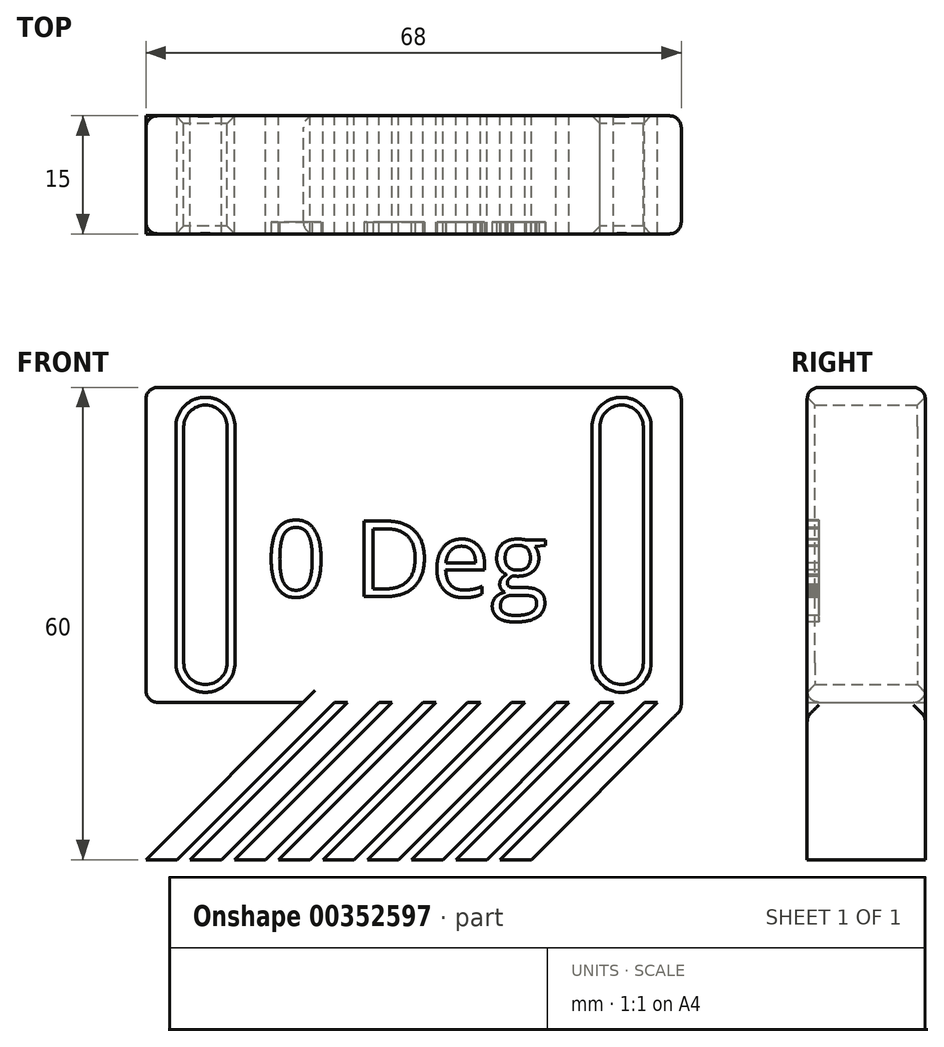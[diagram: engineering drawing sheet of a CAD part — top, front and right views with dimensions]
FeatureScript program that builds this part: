
annotation { "Feature Type Name" : "Feature", "Feature Type Description" : "" }
export const myFeature = defineFeature(function(context is Context, id is Id, definition is map)
    precondition{}
    {
        {
            var Q0;
            Q0=qCreatedBy(makeId("Front.planeOp"),FACE);
            var sketch = newSketch(context, id + "F0", { "sketchPlane" : qUnion([Q0])});
            skLineSegment(sketch, "E0.top", {"start": v(34, 30) * mm, "end": v(-34, 30) * mm});
            skLineSegment(sketch, "E0.left", {"start": v(34, -10.96) * mm, "end": v(34, 30) * mm});
            skLineSegment(sketch, "E0.right", {"start": v(-34, -10) * mm, "end": v(-34, 30) * mm});
            skPoint(sketch, "E0.middle", {"position": v(0, 0) * mm});
            skLineSegment(sketch, "E1", {"start": v(-34, -30) * mm, "end": v(-14, -10) * mm});
            skLineSegment(sketch, "E2", {"start": v(-10.04, -10) * mm, "end": v(-30.04, -30) * mm});
            skLineSegment(sketch, "E3.1.0.0", {"start": v(-28.38, -30) * mm, "end": v(-8.37, -10) * mm});
            skLineSegment(sketch, "E3.1.0.1", {"start": v(-4.42, -10) * mm, "end": v(-24.42, -30) * mm});
            skLineSegment(sketch, "E3.2.0.0", {"start": v(-22.75, -30) * mm, "end": v(-2.75, -10) * mm});
            skLineSegment(sketch, "E3.2.0.1", {"start": v(1.2, -10) * mm, "end": v(-18.8, -30) * mm});
            skLineSegment(sketch, "E3.3.0.0", {"start": v(-17.12, -30) * mm, "end": v(2.88, -10) * mm});
            skLineSegment(sketch, "E3.3.0.1", {"start": v(6.83, -10) * mm, "end": v(-13.17, -30) * mm});
            skLineSegment(sketch, "E3.4.0.0", {"start": v(-11.5, -30) * mm, "end": v(8.5, -10) * mm});
            skLineSegment(sketch, "E3.4.0.1", {"start": v(12.46, -10) * mm, "end": v(-7.54, -30) * mm});
            skLineSegment(sketch, "E3.5.0.0", {"start": v(-5.87, -30) * mm, "end": v(14.13, -10) * mm});
            skLineSegment(sketch, "E3.5.0.1", {"start": v(18.08, -10) * mm, "end": v(-1.92, -30) * mm});
            skLineSegment(sketch, "E3.6.0.0", {"start": v(-0.25, -30) * mm, "end": v(19.75, -10) * mm});
            skLineSegment(sketch, "E3.6.0.1", {"start": v(23.7, -10) * mm, "end": v(3.7, -30) * mm});
            skLineSegment(sketch, "E3.7.0.0", {"start": v(5.38, -30) * mm, "end": v(25.38, -10) * mm});
            skLineSegment(sketch, "E3.7.0.1", {"start": v(29.33, -10) * mm, "end": v(9.33, -30) * mm});
            skLineSegment(sketch, "E3.8.0.0", {"start": v(11, -30) * mm, "end": v(31, -10) * mm});
            skLineSegment(sketch, "E3.8.0.1", {"start": v(34, -10.96) * mm, "end": v(14.96, -30) * mm});
            skLineSegment(sketch, "E3.direction1", {"start": v(-34, -30) * mm, "end": v(-30.04, -30) * mm, "construction": true});
            skLineSegment(sketch, "E4.trimOffspring", {"start": v(-24.42, -30) * mm, "end": v(-28.37, -30) * mm});
            skLineSegment(sketch, "E5.trimOffspring", {"start": v(-30.04, -30) * mm, "end": v(-34, -30) * mm});
            skLineSegment(sketch, "E6.trimOffspring", {"start": v(-18.8, -30) * mm, "end": v(-22.75, -30) * mm});
            skLineSegment(sketch, "E7.trimOffspring", {"start": v(-13.17, -30) * mm, "end": v(-17.12, -30) * mm});
            skLineSegment(sketch, "E8.trimOffspring", {"start": v(-7.54, -30) * mm, "end": v(-11.5, -30) * mm});
            skLineSegment(sketch, "E9.trimOffspring", {"start": v(-1.92, -30) * mm, "end": v(-5.87, -30) * mm});
            skLineSegment(sketch, "E10.trimOffspring", {"start": v(3.7, -30) * mm, "end": v(-0.25, -30) * mm});
            skLineSegment(sketch, "E11.trimOffspring", {"start": v(9.33, -30) * mm, "end": v(5.38, -30) * mm});
            skLineSegment(sketch, "E12.trimOffspring", {"start": v(14.96, -30) * mm, "end": v(11, -30) * mm});
            skPoint(sketch, "E13.orphan", {"position": v(20.58, -30) * mm});
            skPoint(sketch, "E14.orphan", {"position": v(34, -30) * mm});
            skLineSegment(sketch, "E15", {"start": v(-10.04, -10) * mm, "end": v(-8.37, -10) * mm});
            skLineSegment(sketch, "E16.trimOffspring", {"start": v(-4.42, -10) * mm, "end": v(-2.75, -10) * mm});
            skLineSegment(sketch, "E17.trimOffspring", {"start": v(1.2, -10) * mm, "end": v(2.88, -10) * mm});
            skLineSegment(sketch, "E18.trimOffspring", {"start": v(6.83, -10) * mm, "end": v(8.5, -10) * mm});
            skLineSegment(sketch, "E19.trimOffspring", {"start": v(12.46, -10) * mm, "end": v(14.13, -10) * mm});
            skLineSegment(sketch, "E20.trimOffspring", {"start": v(18.08, -10) * mm, "end": v(19.75, -10) * mm});
            skLineSegment(sketch, "E21.trimOffspring", {"start": v(23.7, -10) * mm, "end": v(25.38, -10) * mm});
            skLineSegment(sketch, "E22", {"start": v(-14, -10) * mm, "end": v(-34, -10) * mm});
            skArc(sketch, "E23.0.startCap", {"start": v(-29.19, 25) * mm, "mid": v(-26.44, 27.75) * mm, "end": v(-23.69, 25) * mm});
            skArc(sketch, "E23.0.endCap", {"start": v(-23.69, -5) * mm, "mid": v(-26.44, -7.75) * mm, "end": v(-29.19, -5) * mm});
            skLineSegment(sketch, "E23.0.left", {"start": v(-23.69, 25) * mm, "end": v(-23.69, -5) * mm});
            skLineSegment(sketch, "E23.0.right", {"start": v(-29.19, 25) * mm, "end": v(-29.19, -5) * mm});
            skLineSegment(sketch, "E24.MirrorCS", {"start": v(23.69, 25) * mm, "end": v(23.69, -5) * mm});
            skLineSegment(sketch, "E25.MirrorCS", {"start": v(29.19, 25) * mm, "end": v(29.19, -5) * mm});
            skArc(sketch, "E26.MirrorCS", {"start": v(29.19, 25) * mm, "mid": v(26.44, 27.75) * mm, "end": v(23.69, 25) * mm});
            skArc(sketch, "E27.MirrorCS", {"start": v(23.69, -5) * mm, "mid": v(26.44, -7.75) * mm, "end": v(29.19, -5) * mm});
            skLineSegment(sketch, "E28", {"start": v(29.33, -10) * mm, "end": v(31, -10) * mm});
            skPoint(sketch, "E29.orphan", {"position": v(34.96, -10) * mm});
            skSolve(sketch);
        }
        {
            var Q0;
            Q0 = qSketchRegion(id + "F0", true);
            extrude(context, id + "F1", {"entities" : qUnion([Q0]), "depth" : 15 * mm});
        }
        {
            var Q0;
            Q0=makeQuery(id+"F1.opExtrude","CAP_EDGE",EDGE,{"disambiguationData":[OSD([sQuery(id+"F0.wireOp",EDGE,"E23.0.right")])],"isStart":false});
            var Q1;
            Q1=makeQuery(id+"F1.opExtrude","CAP_EDGE",EDGE,{"disambiguationData":[OSD([sQuery(id+"F0.wireOp",EDGE,"E23.0.left")])],"isStart":true});
            var Q2;
            Q2=makeQuery(id+"F1.opExtrude","CAP_EDGE",EDGE,{"disambiguationData":[OSD([sQuery(id+"F0.wireOp",EDGE,"E25.MirrorCS")])],"isStart":true});
            var Q3;
            Q3=makeQuery(id+"F1.opExtrude","CAP_EDGE",EDGE,{"disambiguationData":[OSD([sQuery(id+"F0.wireOp",EDGE,"E25.MirrorCS")])],"isStart":false});
            chamfer(context, id + "F2", {"entities" : qUnion([Q0, Q1, Q2, Q3]), "width" : 1 * mm, "tangentPropagation" : true});
        }
        {
            var Q0;
            Q0=makeQuery(id+"F1.opExtrude","CAP_EDGE",EDGE,{"disambiguationData":[OSD([sQuery(id+"F0.wireOp",EDGE,"E0.top")])],"isStart":false});
            var Q1;
            Q1=makeQuery(id+"F1.opExtrude","CAP_EDGE",EDGE,{"disambiguationData":[OSD([sQuery(id+"F0.wireOp",EDGE,"E0.right")])],"isStart":false});
            var Q2;
            Q2=makeQuery(id+"F1.opExtrude","CAP_EDGE",EDGE,{"disambiguationData":[OSD([sQuery(id+"F0.wireOp",EDGE,"E0.right")])],"isStart":true});
            var Q3;
            Q3=makeQuery(id+"F1.opExtrude","CAP_EDGE",EDGE,{"disambiguationData":[OSD([sQuery(id+"F0.wireOp",EDGE,"E22")])],"isStart":false});
            var Q4;
            Q4=makeQuery(id+"F1.opExtrude","CAP_EDGE",EDGE,{"disambiguationData":[OSD([sQuery(id+"F0.wireOp",EDGE,"E22")])],"isStart":true});
            var Q5;
            Q5=makeQuery(id+"F1.opExtrude","CAP_EDGE",EDGE,{"disambiguationData":[OSD([sQuery(id+"F0.wireOp",EDGE,"E0.left")])],"isStart":false});
            var Q6;
            Q6=makeQuery(id+"F1.opExtrude","SWEPT_EDGE",EDGE,{"disambiguationData":[OSD([sQuery(id+"F0.wireOp",EDGE,"E0.top"),sQuery(id+"F0.wireOp",EDGE,"E0.left")])]});
            var Q7;
            Q7=makeQuery(id+"F1.opExtrude","SWEPT_EDGE",EDGE,{"disambiguationData":[OSD([sQuery(id+"F0.wireOp",EDGE,"E0.left"),sQuery(id+"F0.wireOp",EDGE,"E3.8.0.1")])]});
            var Q8;
            Q8=makeQuery(id+"F1.opExtrude","CAP_EDGE",EDGE,{"disambiguationData":[OSD([sQuery(id+"F0.wireOp",EDGE,"E0.left")])],"isStart":true});
            var Q9;
            Q9=makeQuery(id+"F1.opExtrude","CAP_EDGE",EDGE,{"disambiguationData":[OSD([sQuery(id+"F0.wireOp",EDGE,"E0.top")])],"isStart":true});
            fillet(context, id + "F3", {"entities" : qUnion([Q0, Q1, Q2, Q3, Q4, Q5, Q6, Q7, Q8, Q9]), "radius" : 1.5 * mm, "tangentPropagation" : true, "allowEdgeOverflow" : false});
        }
        {
            var Q0;
            Q0=makeQuery(id+"F1.opExtrude","SWEPT_EDGE",EDGE,{"disambiguationData":[OSD([sQuery(id+"F0.wireOp",EDGE,"E0.right"),sQuery(id+"F0.wireOp",EDGE,"E22")])]});
            var Q1;
            Q1=makeQuery(id+"F1.opExtrude","SWEPT_EDGE",EDGE,{"disambiguationData":[OSD([sQuery(id+"F0.wireOp",EDGE,"E0.top"),sQuery(id+"F0.wireOp",EDGE,"E0.right")])]});
            fillet(context, id + "F4", {"entities" : qUnion([Q0, Q1]), "radius" : 1.5 * mm, "tangentPropagation" : true, "allowEdgeOverflow" : false});
        }
        {
            var Q0;
            Q0=makeQuery(id+"F3.opFillet","SPLIT",FACE,{"disambiguationData":[OD(1.0)],"derivedFrom":makeQuery(id+"F1.opExtrude","CAP_FACE",FACE,{"disambiguationData":[OSD([sQuery(id+"F0.wireOp",EDGE,"E0.top"),sQuery(id+"F0.wireOp",EDGE,"E0.left"),sQuery(id+"F0.wireOp",EDGE,"E0.right"),sQuery(id+"F0.wireOp",EDGE,"E1"),sQuery(id+"F0.wireOp",EDGE,"E2"),sQuery(id+"F0.wireOp",EDGE,"E3.1.0.0"),sQuery(id+"F0.wireOp",EDGE,"E3.1.0.1"),sQuery(id+"F0.wireOp",EDGE,"E3.2.0.0"),sQuery(id+"F0.wireOp",EDGE,"E3.2.0.1"),sQuery(id+"F0.wireOp",EDGE,"E3.3.0.0"),sQuery(id+"F0.wireOp",EDGE,"E3.3.0.1"),sQuery(id+"F0.wireOp",EDGE,"E3.4.0.0"),sQuery(id+"F0.wireOp",EDGE,"E3.4.0.1"),sQuery(id+"F0.wireOp",EDGE,"E3.5.0.0"),sQuery(id+"F0.wireOp",EDGE,"E3.5.0.1"),sQuery(id+"F0.wireOp",EDGE,"E3.6.0.0"),sQuery(id+"F0.wireOp",EDGE,"E3.6.0.1"),sQuery(id+"F0.wireOp",EDGE,"E3.7.0.0"),sQuery(id+"F0.wireOp",EDGE,"E3.7.0.1"),sQuery(id+"F0.wireOp",EDGE,"E3.8.0.0"),sQuery(id+"F0.wireOp",EDGE,"E3.8.0.1"),sQuery(id+"F0.wireOp",EDGE,"E4.trimOffspring"),sQuery(id+"F0.wireOp",EDGE,"E5.trimOffspring"),sQuery(id+"F0.wireOp",EDGE,"E6.trimOffspring"),sQuery(id+"F0.wireOp",EDGE,"E7.trimOffspring"),sQuery(id+"F0.wireOp",EDGE,"E8.trimOffspring"),sQuery(id+"F0.wireOp",EDGE,"E9.trimOffspring"),sQuery(id+"F0.wireOp",EDGE,"E10.trimOffspring"),sQuery(id+"F0.wireOp",EDGE,"E11.trimOffspring"),sQuery(id+"F0.wireOp",EDGE,"E12.trimOffspring"),sQuery(id+"F0.wireOp",EDGE,"E15"),sQuery(id+"F0.wireOp",EDGE,"E16.trimOffspring"),sQuery(id+"F0.wireOp",EDGE,"E17.trimOffspring"),sQuery(id+"F0.wireOp",EDGE,"E18.trimOffspring"),sQuery(id+"F0.wireOp",EDGE,"E19.trimOffspring"),sQuery(id+"F0.wireOp",EDGE,"E20.trimOffspring"),sQuery(id+"F0.wireOp",EDGE,"E21.trimOffspring"),sQuery(id+"F0.wireOp",EDGE,"E22"),sQuery(id+"F0.wireOp",EDGE,"E23.0.startCap"),sQuery(id+"F0.wireOp",EDGE,"E23.0.endCap"),sQuery(id+"F0.wireOp",EDGE,"E23.0.left"),sQuery(id+"F0.wireOp",EDGE,"E23.0.right"),sQuery(id+"F0.wireOp",EDGE,"E24.MirrorCS"),sQuery(id+"F0.wireOp",EDGE,"E25.MirrorCS"),sQuery(id+"F0.wireOp",EDGE,"E26.MirrorCS"),sQuery(id+"F0.wireOp",EDGE,"E27.MirrorCS"),sQuery(id+"F0.wireOp",EDGE,"E28")])],"isStart":false})});
            var sketch = newSketch(context, id + "F5", { "sketchPlane" : qUnion([Q0])});
            skText(sketch, "E30", { "text": "0 Deg", "fontName": "OpenSans-Regular.ttf"});
            const initialGuessF5  = {"E30": [-0.01876, 0.00342, 1, 0, 0.00967]};
            skSetInitialGuess(sketch, initialGuessF5);
            skSolve(sketch);
        }
        {
            var Q0;
            Q0 = qSketchRegion(id + "F5", true);
            extrude(context, id + "F6", {"entities" : qUnion([Q0]), "operationType" : NewBodyOperationType.REMOVE, "oppositeDirection" : true, "depth" : 1.5 * mm});
        }
    });
